# Revit family: PRE030004
name_source: partatom
category: Appareils sanitaires
revit_build: Autodesk Revit 2015 (Build: 20140606_1530(x64)
units: mm (PartAtom-declared; Revit-internal decimal feet)

## types (1)
- MasterMix New
    Adresse du fabricant = 7 RUE RACINE  92542 MONTROUGE CEDEX FRANCE
    Corps = PRESTO Chromé
    Diamètre nominal = 15 mm  [stored 0.0492126 ft]
    Débit = Regle usine a 9L/min a 3 bar
    Elévation par défaut = 0 mm  [stored 0 ft]
    Finition = Boitier metal injecte poli chrome + Capots dextremite en ABS haute resistance RAL 9003
    Fonction = -
    Garantie = 10 ans contre tout vice de fabrication / 3 ans pour la cartouche thermostatique
    Hauteur nominale = -
    Lien CCTP = http://www.prestodatashare.com
    Lien données techniques = http://www.prestodatashare.com
    Lien site internet = http://www.prestodatashare.com
    Longueur nominale = -
    Nom = 75702 Presto Mitigeur thermostatique de douche MASTERMIX  Applique sortie haute
    Partie supérieure = PRESTO Blanc
    Pertes de charge = 100.0 Pa
    Polantis code = PRE030004
    Pression = 1 a 5 bars
    Profondeur nominale = -
    Robinetterie = PRESTO Laiton chromé
    Référence = 75702
    Type de raccordement = G 1/2'' - EA150+/-10
    URL fabricant = http://www.prestodatashare.com
    Version = 15

note: [stored X ft] marks values corroborated as IEEE doubles in the binary element streams (Revit-internal decimal feet)

## geometry (parser evidence)
native form markers: Blend x2, Sweep x19
no freeform markers — native parametric forms only
